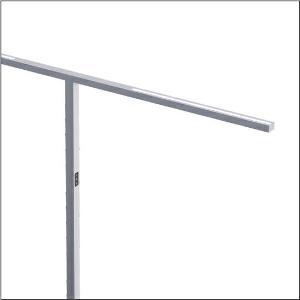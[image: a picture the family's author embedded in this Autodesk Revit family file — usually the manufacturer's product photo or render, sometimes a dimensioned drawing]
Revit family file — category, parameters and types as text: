
# Revit family: silica_r__31_floor_duo_51my52hmtcs_b166
name_source: partatom
category: Lighting Fixtures
units: mm (PartAtom-declared; Revit-internal decimal feet)

## family parameters
Cut with Voids When Loaded = No
Host = Face
Light Source = No
Part Type = Normal
Room Calculation Point = No
Round Connector Dimension = Use Diameter
Shared = No

## types (1)
- --- (1 x LED, 17040 lm, 142 W, 4000K)
    Apparent Load = 142 VA
    CIE Flux Codes = 86 100 100 24 100
    Color Rendering = 80
    Color Temperature = 4000K
    Default Elevation = 1800 mm
    Description = Silica® 31 Floor duo, floorstanding luminaire, secondary optical cover: cover panel, of PMMA, light emission: direct/indirect distribution, primary light characteristic: symmetric, installation type: not mounted, LED, rated luminous flux: 17.040lm, luminous efficacy: 120lm/W, light colour: 8tw, colour temperature: 2700..6500K, daylight-dependent control, with cable with plug, mains connection: 230V, AC, 50Hz, rated input power: 142W, luminaire head, of aluminium, coated, metallic grey (RAL 9006), length: 2.372mm, width: 52mm, supporting column, angular, of aluminium, coated, silver, baseplate, of steel, coated, metallic grey (RAL 9006), protection rating (complete): IP20, insulation class (complete): insulation class I (protective earthing), certification: CE, permissible operating ambient temperature: -20..+40°C, standard: EN 50419, packaging unit: 1 piece
    Height = 36 mm
    Lamp = 1 x LED
    Lamp Light Flux = 17040 lm
    Lamp Power = 142 W
    Lamp count = 1
    Length = 2372 mm
    Luminous efficacy = 120 lm/W
    Manufacturer = Siteco
    ModVariant = No
    Model = 51MY52HMTCS
    Mounting Place = Floor
    Mounting Type = Freestanding
    Number of Poles = 1
    OnlyDefault = Yes
    Power Factor = 1
    Product Name = Silica® 31 Floor duo
    Product group = floorstanding luminaire
    ProductGroupID = 1301
    Protection Class = Protection class I
    Protection Degree = IP 20
    RLX_Detail_Level = 1
    RLX_Emergency_Light_Flux = 0 lm
    RLX_Emergency_Type = 0
    RLX_Emergency_Type_DB = No
    RlxData = <blob elided: 17777 chars, md5=7212e05e>
    Socket = socket
    Standby Power = 0 W
    System Light Flux = 17040 lm
    System Power = 142 W
    Type Comments = factory setting
    Type Image = l_1275342.jpg
    URL = http://relux.com
    VarID = @adj_032429
    Voltage = 0 V
    Weight = 0.00 kg
    Width = 52 mm  [stored 0.170604 ft]

note: [stored X ft] marks values corroborated as IEEE doubles in the binary element streams (Revit-internal decimal feet)

## geometry (parser evidence)
native form markers: Blend x4, Sweep x13
no freeform markers — native parametric forms only
